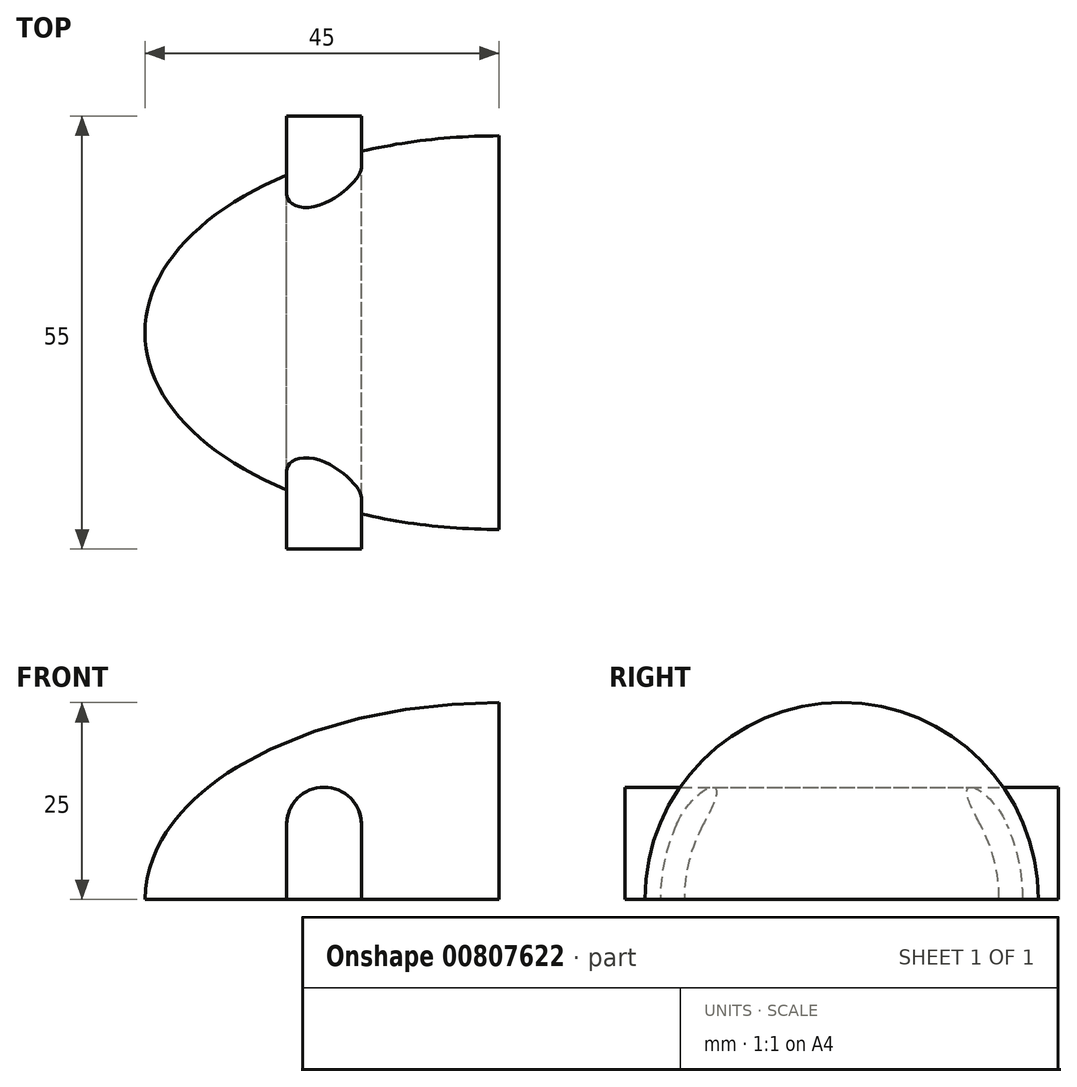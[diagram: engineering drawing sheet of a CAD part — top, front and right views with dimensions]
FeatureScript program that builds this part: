
annotation { "Feature Type Name" : "Feature", "Feature Type Description" : "" }
export const myFeature = defineFeature(function(context is Context, id is Id, definition is map)
    precondition{}
    {
        {
            var Q0;
            Q0=qCreatedBy(makeId("Front.planeOp"),FACE);
            var sketch = newSketch(context, id + "F0", { "sketchPlane" : qUnion([Q0])});
            skEllipticalArc(sketch, "E0", {});
            skLineSegment(sketch, "E1", {"start": v(-45, 0) * mm, "end": v(0, 0) * mm});
            skLineSegment(sketch, "E2", {"start": v(0, 0) * mm, "end": v(0, 25) * mm});
            skPoint(sketch, "E3.orphan", {"position": v(0, -6.13) * mm});
            skPoint(sketch, "E4.orphan", {"position": v(-59, 0) * mm});
            skLineSegment(sketch, "E5", {"start": v(0, 0) * mm, "end": v(-59, 0) * mm, "construction": true});
            const initialGuessF0  = {"E0": [0, 0, -1, 0, 0.045, 0.025, 4.71238898038469, 0]};
            skSetInitialGuess(sketch, initialGuessF0);
            skSolve(sketch);
        }
        {
            var Q0;
            Q0 = qSketchRegion(id + "F0", true);
            var Q1;
            Q1=sQuery(id+"F0.wireOp",EDGE,"E1");
            revolve(context, id + "F1", {"surfaceOperationType" : NewSurfaceOperationType.NEW, "entities" : qUnion([Q0]), "axis" : qUnion([Q1]), "revolveType" : RevolveType.SYMMETRIC, "angle" : 180 * degree});
        }
        {
            var Q0;
            Q0=qCreatedBy(makeId("Front.planeOp"),FACE);
            var sketch = newSketch(context, id + "F2", { "sketchPlane" : qUnion([Q0])});
            skLineSegment(sketch, "E6.bottom", {"start": v(-27, 0) * mm, "end": v(-17.5, 0) * mm});
            skLineSegment(sketch, "E6.top", {"start": v(-27, 9.5) * mm, "end": v(-17.5, 9.5) * mm});
            skLineSegment(sketch, "E6.left", {"start": v(-27, 0) * mm, "end": v(-27, 9.5) * mm});
            skLineSegment(sketch, "E6.right", {"start": v(-17.5, 0) * mm, "end": v(-17.5, 9.5) * mm});
            skArc(sketch, "E7", {"start": v(-27, 9.5) * mm, "mid": v(-22.25, 14.25) * mm, "end": v(-17.5, 9.5) * mm});
            skSolve(sketch);
        }
        {
            var Q0;
            Q0 = qSketchRegion(id + "F2", true);
            extrude(context, id + "F3", {"entities" : qUnion([Q0]), "depth" : 55 * mm, "offsetDistance" : 25 * mm, "symmetric" : true});
        }
        {
            var Q0;
            Q0=makeQuery(id+"F3.opExtrude","SWEPT_BODY",BODY,{"disambiguationData":[OSD([sQuery(id+"F2.wireOp",EDGE,"E6.bottom"),sQuery(id+"F2.wireOp",EDGE,"E6.left"),sQuery(id+"F2.wireOp",EDGE,"E6.right"),sQuery(id+"F2.wireOp",EDGE,"E7")])]});
            var Q1;
            Q1=makeQuery(id+"F1.opRevolve","SWEPT_BODY",BODY,{"disambiguationData":[OSD([sQuery(id+"F0.wireOp",EDGE,"E0"),sQuery(id+"F0.wireOp",EDGE,"E1"),sQuery(id+"F0.wireOp",EDGE,"E2")])]});
            booleanBodies(context, id + "F4", {"operationType" : BooleanOperationType.SUBTRACTION, "tools" : qUnion([Q0]), "targets" : qUnion([Q1]), "keepTools" : true});
        }
    });
